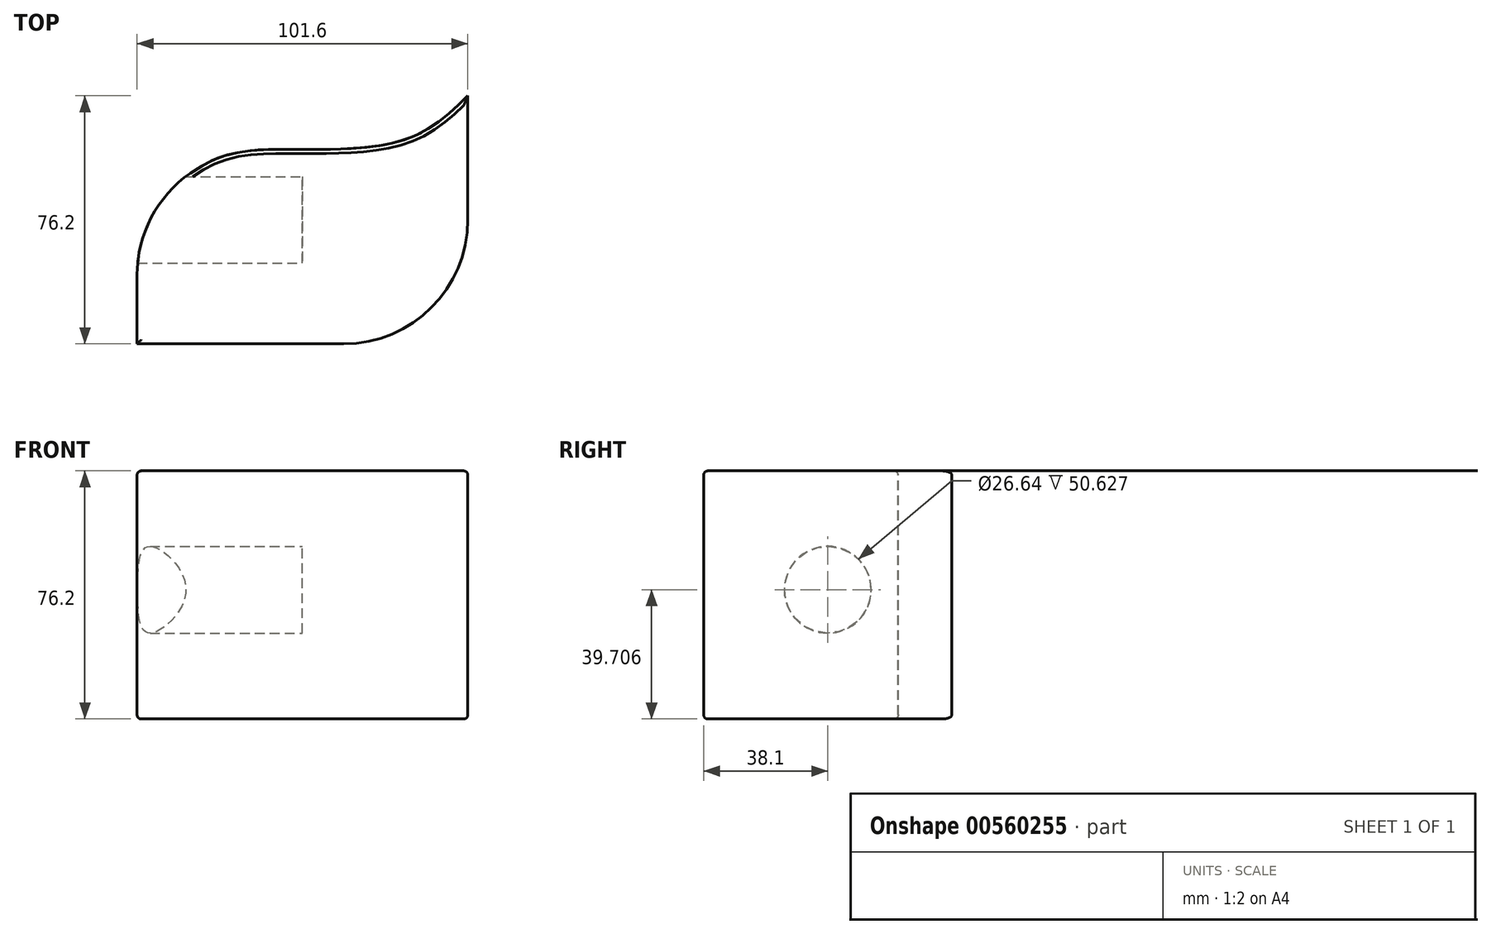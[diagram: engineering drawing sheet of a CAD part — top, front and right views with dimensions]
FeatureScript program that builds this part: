
annotation { "Feature Type Name" : "Feature", "Feature Type Description" : "" }
export const myFeature = defineFeature(function(context is Context, id is Id, definition is map)
    precondition{}
    {
        {
            var Q0;
            Q0=qCreatedBy(makeId("Top.planeOp"),FACE);
            var sketch = newSketch(context, id + "F0", { "sketchPlane" : qUnion([Q0])});
            skLineSegment(sketch, "E0.bottom", {"start": v(50.8, 38.1) * mm, "end": v(-50.8, 38.1) * mm});
            skLineSegment(sketch, "E0.top", {"start": v(50.8, -38.1) * mm, "end": v(-50.8, -38.1) * mm});
            skLineSegment(sketch, "E0.left", {"start": v(50.8, 38.1) * mm, "end": v(50.8, -38.1) * mm});
            skLineSegment(sketch, "E0.right", {"start": v(-50.8, 38.1) * mm, "end": v(-50.8, -38.1) * mm});
            skPoint(sketch, "E0.middle", {"position": v(0, 0) * mm});
            skFitSpline(sketch, "E1", {"points": [v(-50.8, 0) * mm, v(-26.56, 18.73) * mm, v(0, 21.63) * mm, v(33.03, 25.2) * mm, v(50.8, 38.1) * mm], "startDerivative": vector(89.91, 87.24) * mm, "endDerivative": vector(69.68, 68.13) * mm});
            skSolve(sketch);
        }
        {
            var Q0;
            {var subQ0=sQuery(id+"F0.wireOp",EDGE,"E0.top");Q0=makeQuery(id+"F0.imprint","IMPRINT",FACE,{"disambiguationData":[TD([[makeQuery(id+"F0.imprint","IMPRINT",EDGE,{"derivedFrom":subQ0}),-1.0]])]});}
            extrude(context, id + "F1", {"entities" : qUnion([Q0]), "depth" : 76.2 * mm, "offsetDistance" : 25.4 * mm});
        }
        {
            var Q0;
            Q0=makeQuery(id+"F1.opExtrude","SWEPT_EDGE",EDGE,{"disambiguationData":[OSD([sQuery(id+"F0.wireOp",EDGE,"E0.top"),sQuery(id+"F0.wireOp",EDGE,"E0.left")])]});
            var Q1;
            Q1=makeQuery(id+"F1.opExtrude","SWEPT_EDGE",EDGE,{"disambiguationData":[OSD([sQuery(id+"F0.wireOp",EDGE,"E0.right"),sQuery(id+"F0.wireOp",EDGE,"E1")])]});
            fillet(context, id + "F2", {"entities" : qUnion([Q0, Q1]), "radius" : 38.1 * mm, "tangentPropagation" : true, "allowEdgeOverflow" : false});
        }
        {
            var Q0;
            Q0=makeQuery(id+"F1.opExtrude","CAP_EDGE",EDGE,{"disambiguationData":[OSD([sQuery(id+"F0.wireOp",EDGE,"E1")])],"isStart":false});
            var Q1;
            Q1=makeQuery(id+"F1.opExtrude","CAP_EDGE",EDGE,{"disambiguationData":[OSD([sQuery(id+"F0.wireOp",EDGE,"E0.top")])],"isStart":false});
            var Q2;
            {var subQ0=sQuery(id+"F0.wireOp",EDGE,"E0.left");var subQ1=sQuery(id+"F0.wireOp",EDGE,"E0.top");Q2=makeQuery(id+"F2.opFillet","BLEND_EDGE",EDGE,{"blendedFrom":[makeQuery(id+"F1.opExtrude","SWEPT_EDGE",EDGE,{"disambiguationData":[OSD([subQ1,subQ0])]}),makeQuery(id+"F1.opExtrude","CAP_FACE",FACE,{"disambiguationData":[OSD([subQ1,subQ0,sQuery(id+"F0.wireOp",EDGE,"E0.right"),sQuery(id+"F0.wireOp",EDGE,"E1")])],"isStart":false})],"blendedInto":[makeQuery(id+"F1.opExtrude","CAP_FACE",FACE,{"disambiguationData":[OSD([subQ1,subQ0,sQuery(id+"F0.wireOp",EDGE,"E0.right"),sQuery(id+"F0.wireOp",EDGE,"E1")])],"isStart":false})]});}
            var Q3;
            Q3=makeQuery(id+"F1.opExtrude","CAP_EDGE",EDGE,{"disambiguationData":[OSD([sQuery(id+"F0.wireOp",EDGE,"E0.top")])],"isStart":true});
            var Q4;
            Q4=makeQuery(id+"F1.opExtrude","CAP_EDGE",EDGE,{"disambiguationData":[OSD([sQuery(id+"F0.wireOp",EDGE,"E1")])],"isStart":true});
            fillet(context, id + "F3", {"entities" : qUnion([Q0, Q1, Q2, Q3, Q4]), "radius" : 1.27 * mm, "tangentPropagation" : true, "allowEdgeOverflow" : false});
        }
        {
            var Q0;
            Q0=qCreatedBy(makeId("Right.planeOp"),FACE);
            var sketch = newSketch(context, id + "F4", { "sketchPlane" : qUnion([Q0])});
            skCircle(sketch, "E2", {"center": v(0, 39.7) * mm, "radius": 13.32 * mm});
            skSolve(sketch);
        }
        {
            var Q0;
            Q0 = qSketchRegion(id + "F4", true);
            extrude(context, id + "F5", {"entities" : qUnion([Q0]), "operationType" : NewBodyOperationType.REMOVE, "endBound" : BoundingType.THROUGH_ALL, "oppositeDirection" : true, "depth" : 25.4 * mm, "offsetDistance" : 25.4 * mm});
        }
    });
